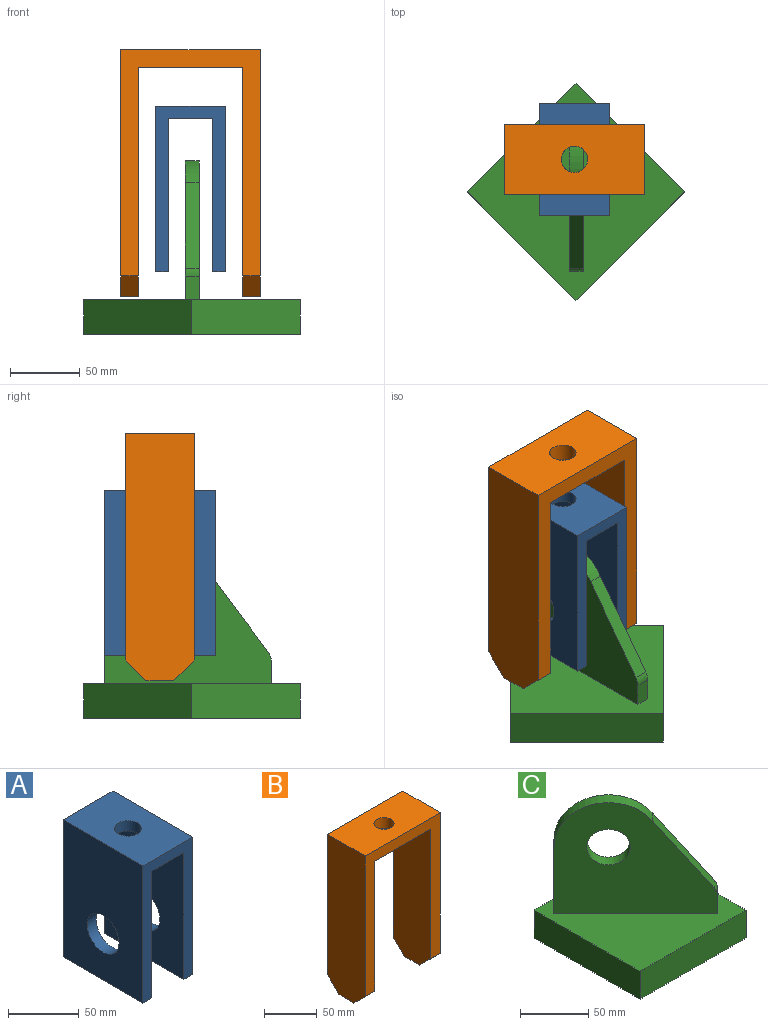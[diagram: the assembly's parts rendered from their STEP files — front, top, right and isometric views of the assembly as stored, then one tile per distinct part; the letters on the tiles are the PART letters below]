
ASSEMBLY  parts=3 mates=4
PART A: 13 faces, bbox 50x80x119 mm
  f0: plane 119x80mm, normal (-1,0,0), area 8715.8mm2, adj f1,f7,f8,f9,f11
  f1: plane 80x9mm, normal (0,0,-1), area 720mm2, adj f0,f2,f8,f9
  f2: plane 110x80mm, normal (1,0,0), area 7995.8mm2, adj f1,f3,f8,f9,f11
  f3: plane 80x32mm, normal (0,0,-1), area 2276.5mm2, adj f2,f4,f8,f9,f12
  f4: plane 110x80mm, normal (-1,0,0), area 7995.8mm2, adj f3,f5,f8,f9,f10
  f5: plane 80x9mm, normal (0,0,-1), area 720mm2, adj f4,f6,f8,f9
  f6: plane 119x80mm, normal (1,0,0), area 8715.8mm2, adj f5,f7,f8,f9,f10
  f7: plane 80x50mm, normal (0,0,1), area 3716.5mm2, adj f0,f6,f8,f9,f12
  f8: plane 119x50mm, normal (0,-1,0), area 2430mm2, adj f0,f1,f2,f3,f4,f5,f6,f7
  f9: plane 119x50mm, normal (0,1,0), area 2430mm2, adj f0,f1,f2,f3,f4,f5,f6,f7
  f10: cylinder r=16mm len=32mm, axis (-1,0,0), area 904.8mm2, adj f4,f6
  f11: cylinder r=16mm len=32mm, axis (-1,0,0), area 904.8mm2, adj f0,f2
  f12: cylinder r=9.5mm len=19mm, axis (0,0,1), area 537.2mm2, adj f3,f7
PART B: 15 faces, bbox 100.4x50x177.7 mm
  f0: plane 20x12.7mm, normal (0,0,-1), area 254mm2, adj f1,f7,f11,f12
  f1: plane 165x50mm, normal (1,0,0), area 8025mm2, adj f0,f2,f8,f9,f11,f12
  f2: plane 75x50mm, normal (0,0,-1), area 3466.5mm2, adj f1,f3,f8,f9,f10
  f3: plane 165x50mm, normal (-1,0,0), area 8025mm2, adj f2,f4,f8,f9,f13,f14
  f4: plane 20x12.7mm, normal (0,0,-1), area 254mm2, adj f3,f5,f13,f14
  f5: plane 177.7x50mm, normal (1,0,0), area 8660mm2, adj f4,f6,f8,f9,f13,f14
  f6: plane 100.4x50mm, normal (0,0,1), area 4736.5mm2, adj f5,f7,f8,f9,f10
  f7: plane 177.7x50mm, normal (-1,0,0), area 8660mm2, adj f0,f6,f8,f9,f11,f12
  f8: plane 162.7x100.4mm, normal (0,-1,0), area 5085.1mm2, adj f1,f2,f3,f5,f6,f7,f12,f14
  f9: plane 162.7x100.4mm, normal (0,1,0), area 5085.1mm2, adj f1,f2,f3,f5,f6,f7,f11,f13
  f10: cylinder r=9.5mm len=19mm, axis (0,0,1), area 758.1mm2, adj f2,f6
  f11: plane 15x15mm, normal (0,0.71,-0.71), area 269.4mm2, adj f0,f1,f7,f9
  f12: plane 15x15mm, normal (0,-0.71,-0.71), area 269.4mm2, adj f0,f1,f7,f8
  f13: plane 15x15mm, normal (0,0.71,-0.71), area 269.4mm2, adj f3,f4,f5,f9
  f14: plane 15x15mm, normal (0,-0.71,-0.71), area 269.4mm2, adj f3,f4,f5,f8
PART C: 14 faces, bbox 110x110x125 mm
  f0: plane 100x84.85mm, normal (0.71,0.71,0), area 8393.1mm2, adj f2,f7,f9,f10,f11,f12,f13
  f1: plane 100x84.85mm, normal (-0.71,-0.71,0), area 8393.1mm2, adj f2,f7,f9,f10,f11,f12,f13
  f2: plane 16.67x7.07mm, normal (0.71,-0.71,0), area 166.7mm2, adj f0,f1,f7,f12
  f3: plane 110x25mm, normal (0,1,0), area 2750mm2, adj f4,f6,f7,f8
  f4: plane 110x25mm, normal (-1,0,0), area 2750mm2, adj f3,f5,f7,f8
  f5: plane 110x25mm, normal (0,-1,0), area 2750mm2, adj f4,f6,f7,f8
  f6: plane 110x25mm, normal (1,0,0), area 2750mm2, adj f3,f5,f7,f8
  f7: plane 110x110mm, normal (0,0,1), area 10900mm2, adj f0,f1,f2,f3,f4,f5,f6,f9
  f8: plane 110x110mm, normal (0,0,-1), area 12100mm2, adj f3,f4,f5,f6
  f9: plane 60x7.07mm, normal (-0.71,0.71,0), area 600mm2, adj f0,f1,f7,f11
  f10: plane 61.33x39.6mm, normal (0.57,-0.57,0.6), area 766.7mm2, adj f0,f1,f11,f12
  f11: cylinder r=40mm len=57.98mm, axis (0.71,0.71,0), area 999.2mm2, adj f0,f1,f9,f10
  f12: cylinder r=10mm len=8.49mm, axis (0.71,0.71,0), area 64.4mm2, adj f0,f1,f2,f10
  f13: cylinder r=16mm len=32mm, axis (0.71,0.71,0), area 1005.3mm2, adj f0,f1
PLACE A t=(-1.27,-40.8,-122.94)mm
PLACE B rot(axis=(0,0,-1),180deg) t=(44.05,-105.8,-114.62)mm
PLACE C rot(axis=(0,0,-1),45deg) t=(-82.86,-103.94,-141.64)mm fixed
MATE parallel B.f8 <-> C.f9  axis (0,1,0) through (-6.15,-55.8,-4.22)mm
MATE parallel C.f7 <-> A.f5  axis (0,0,1) through (33.82,-65.05,-116.64)mm
MATE cylindrical A.f12 <-> B.f10  axis (0,0,1) through (-6.15,-80.8,22.36)mm
MATE cylindrical C.f11 <-> A.f10  axis (1,0,0) through (-4.86,-80.8,-56.64)mm
